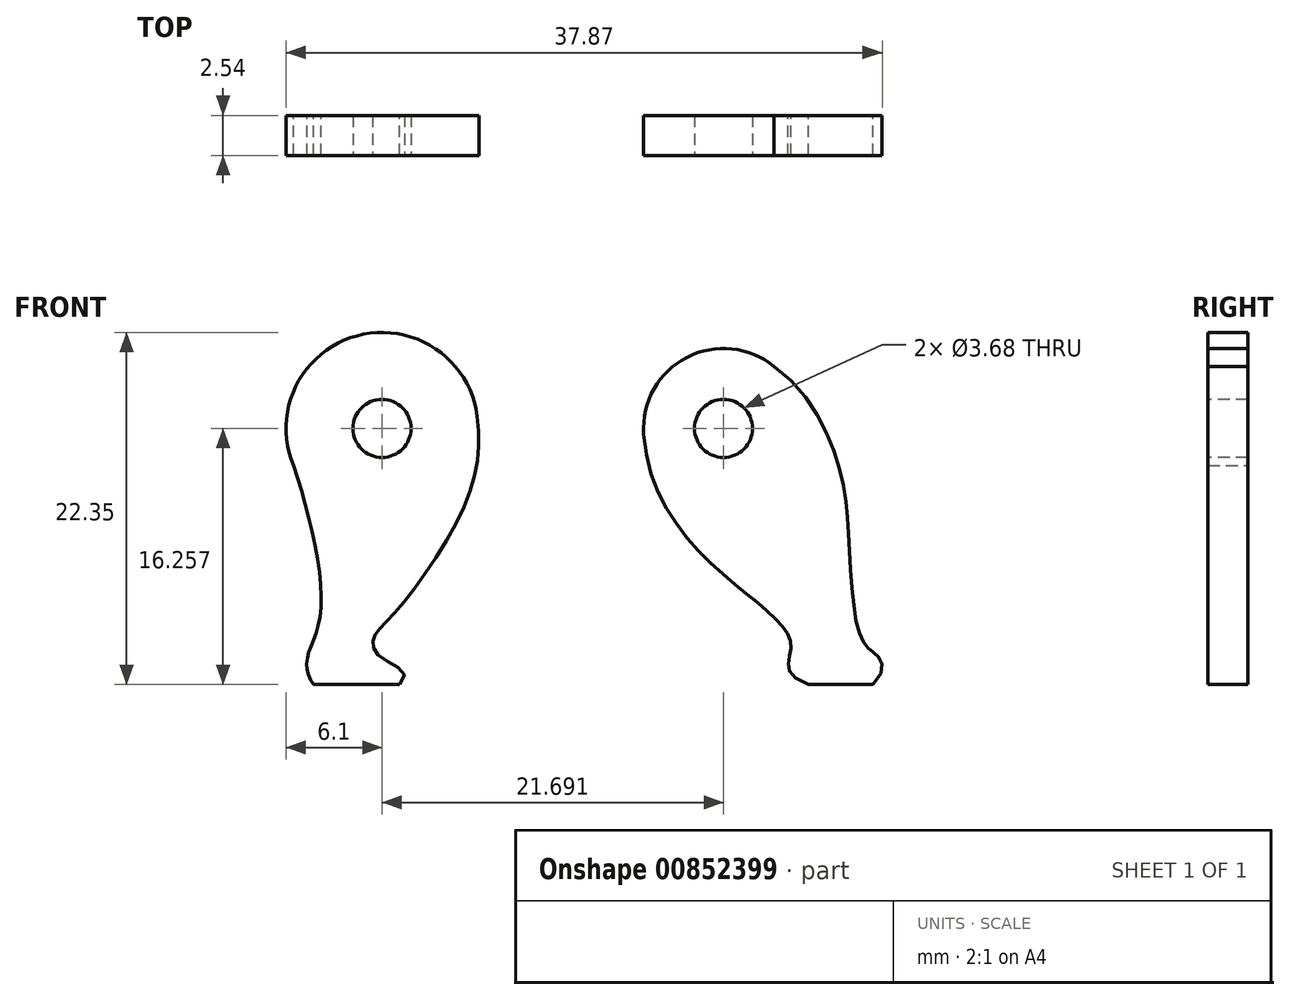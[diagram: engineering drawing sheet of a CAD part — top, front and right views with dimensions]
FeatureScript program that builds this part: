
annotation { "Feature Type Name" : "Feature", "Feature Type Description" : "" }
export const myFeature = defineFeature(function(context is Context, id is Id, definition is map)
    precondition{}
    {
        {
            var Q0;
            Q0=qCreatedBy(makeId("Front.planeOp"),FACE);
            var sketch = newSketch(context, id + "F0", { "sketchPlane" : qUnion([Q0])});
            skPoint(sketch, "E0", {"position": v(11.26, 4.26) * mm});
            skPoint(sketch, "E1", {"position": v(-15.85, 4.26) * mm});
            skCircle(sketch, "E2", {"center": v(11.26, 4.26) * mm, "radius": 1.27 * mm, "construction": true});
            skCircle(sketch, "E3", {"center": v(-15.85, 4.26) * mm, "radius": 1.27 * mm, "construction": true});
            skArc(sketch, "E4.0", {"start": v(15.28, 9.18) * mm, "mid": v(8.35, 9.9) * mm, "end": v(4.93, 3.84) * mm});
            skArc(sketch, "E5.0", {"start": v(-8.3, 5.24) * mm, "mid": v(-17.84, 11.61) * mm, "end": v(-22.87, 1.3) * mm});
            skLineSegment(sketch, "E6", {"start": v(-29.33, -16.06) * mm, "end": v(27.76, -16.06) * mm, "construction": true});
            skFitSpline(sketch, "E7", {"points": [v(-22.87, 1.3) * mm, v(-20.73, -10.44) * mm, v(-21.79, -14.03) * mm, v(-21.3, -16.06) * mm], "startDerivative": vector(7.23, -21.38) * mm, "endDerivative": vector(5.9, -7.29) * mm});
            skFitSpline(sketch, "E8", {"points": [v(-8.3, 5.24) * mm, v(-9.33, -1.9) * mm, v(-14.9, -10.43) * mm, v(-16.53, -12.43) * mm, v(-15.85, -13.96) * mm, v(-14.44, -16.06) * mm], "startDerivative": vector(3.6, -27.83) * mm, "endDerivative": vector(-22.12, -19.6) * mm});
            skFitSpline(sketch, "E9", {"points": [v(4.93, 3.84) * mm, v(13.3, -9.04) * mm, v(16.64, -13.1) * mm, v(18.01, -16.06) * mm], "startDerivative": vector(2.58, -39.4) * mm, "endDerivative": vector(32.1, -10.9) * mm});
            skPoint(sketch, "E10.1.internal.snap0", {"position": v(20.43, 4.5) * mm});
            skFitSpline(sketch, "E10", {"points": [v(15.28, 9.18) * mm, v(20.43, 1.2) * mm, v(21.25, -5.04) * mm, v(21.94, -11.66) * mm, v(22.83, -13.26) * mm, v(23.64, -13.99) * mm, v(23.11, -16.06) * mm], "startDerivative": vector(33.67, -23.57) * mm, "endDerivative": vector(-23, -20.31) * mm});
            skLineSegment(sketch, "E11", {"start": v(-21.3, -16.06) * mm, "end": v(-14.44, -16.06) * mm});
            skLineSegment(sketch, "E12", {"start": v(18.01, -16.06) * mm, "end": v(23.11, -16.06) * mm});
            skCircle(sketch, "E13", {"center": v(-15.85, 4.26) * mm, "radius": 1.9 * mm});
            skCircle(sketch, "E14", {"center": v(11.26, 4.26) * mm, "radius": 1.9 * mm});
            skLineSegment(sketch, "E15", {"start": v(-15.85, 4.26) * mm, "end": v(-15.85, -16.06) * mm, "construction": true});
            skLineSegment(sketch, "E16", {"start": v(11.26, 4.26) * mm, "end": v(11.26, -16.06) * mm, "construction": true});
            skSolve(sketch);
        }
        {
            var Q0;
            Q0=qSketchRegion(id+"F0",true);
            extrude(context, id + "F1", {"entities" : qUnion([Q0]), "depth" : 3.17 * mm});
        }
        {
            var Q0;
            Q0=makeQuery(id+"F1.opExtrude","SWEPT_BODY",BODY,{"disambiguationData":[OSD([sQuery(id+"F0.wireOp",EDGE,"E4.0"),sQuery(id+"F0.wireOp",EDGE,"E9"),sQuery(id+"F0.wireOp",EDGE,"E10"),sQuery(id+"F0.wireOp",EDGE,"E12"),sQuery(id+"F0.wireOp",EDGE,"E14")])]});
            var Q1;
            Q1=makeQuery(id+"F1.opExtrude","SWEPT_BODY",BODY,{"disambiguationData":[OSD([sQuery(id+"F0.wireOp",EDGE,"E5.0"),sQuery(id+"F0.wireOp",EDGE,"E7"),sQuery(id+"F0.wireOp",EDGE,"E8"),sQuery(id+"F0.wireOp",EDGE,"E11"),sQuery(id+"F0.wireOp",EDGE,"E13")])]});
            var Q2;
            Q2=qCreatedBy(makeId("Origin.pointOp"),VERTEX);
            transform(context, id + "F2", {"entities" : qUnion([Q0, Q1]), "transformType" : TransformType.SCALE_UNIFORMLY, "scale" : 0.8, "scalePoint" : qUnion([Q2]), "makeCopy" : false});
        }
        {
            var Q0;
            Q0=makeQuery(id+"F1.opExtrude","CAP_FACE",FACE,{"disambiguationData":[OSD([sQuery(id+"F0.wireOp",EDGE,"E5.0"),sQuery(id+"F0.wireOp",EDGE,"E7"),sQuery(id+"F0.wireOp",EDGE,"E8"),sQuery(id+"F0.wireOp",EDGE,"E11"),sQuery(id+"F0.wireOp",EDGE,"E13")])],"isStart":false});
            var sketch = newSketch(context, id + "F3", { "sketchPlane" : qUnion([Q0])});
            skCircle(sketch, "E17.0", {"center": v(-12.68, 3.4) * mm, "radius": 1.52 * mm, "construction": true});
            skCircle(sketch, "E18.0", {"center": v(9.01, 3.4) * mm, "radius": 1.52 * mm, "construction": true});
            skCircle(sketch, "E19", {"center": v(-12.68, 3.4) * mm, "radius": 1.84 * mm});
            skCircle(sketch, "E20", {"center": v(9.01, 3.4) * mm, "radius": 1.84 * mm});
            skSolve(sketch);
        }
        {
            var Q0;
            Q0=qSketchRegion(id+"F3",true);
            extrude(context, id + "F4", {"entities" : qUnion([Q0]), "operationType" : NewBodyOperationType.REMOVE, "endBound" : BoundingType.THROUGH_ALL, "oppositeDirection" : true, "depth" : 25.4 * mm});
        }
    });
